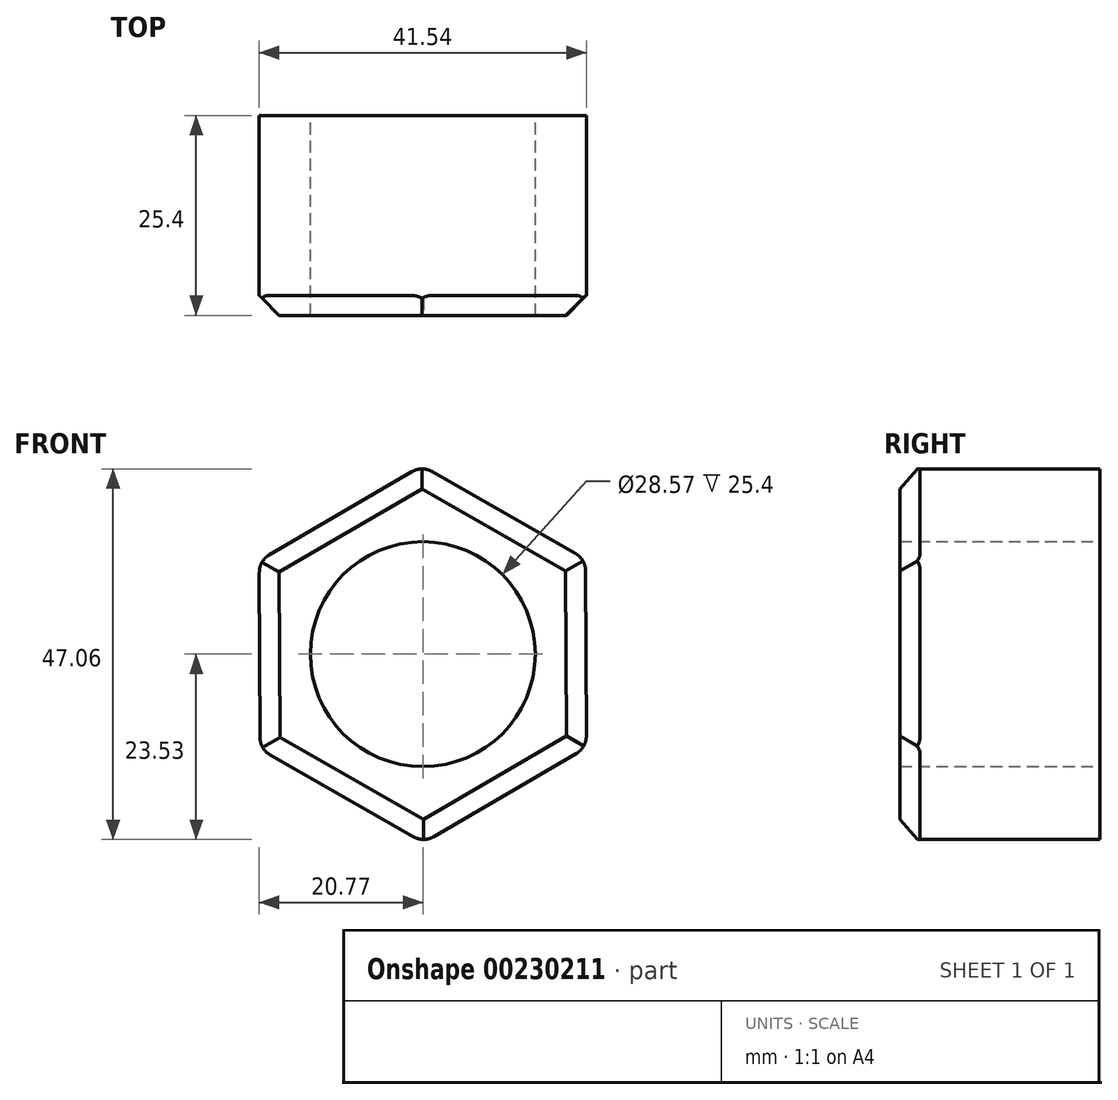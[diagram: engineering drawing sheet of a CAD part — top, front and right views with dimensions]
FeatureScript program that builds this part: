
annotation { "Feature Type Name" : "Feature", "Feature Type Description" : "" }
export const myFeature = defineFeature(function(context is Context, id is Id, definition is map)
    precondition{}
    {
        {
            var Q0;
            Q0=qCreatedBy(makeId("Front.planeOp"),FACE);
            var sketch = newSketch(context, id + "F0", { "sketchPlane" : qUnion([Q0])});
            skCircle(sketch, "E0", {"center": v(0, 0) * mm, "radius": 14.29 * mm});
            skCircle(sketch, "E1.cCircle", {"center": v(0, 0) * mm, "radius": 20.72 * mm, "construction": true});
            skLineSegment(sketch, "E1.0", {"start": v(-0.1, 23.93) * mm, "end": v(20.67, 12.06) * mm});
            skLineSegment(sketch, "E1.1", {"start": v(20.67, 12.06) * mm, "end": v(20.77, -11.87) * mm});
            skLineSegment(sketch, "E1.2", {"start": v(20.77, -11.87) * mm, "end": v(0.1, -23.93) * mm});
            skLineSegment(sketch, "E1.3", {"start": v(0.1, -23.93) * mm, "end": v(-20.67, -12.06) * mm});
            skLineSegment(sketch, "E1.4", {"start": v(-20.67, -12.06) * mm, "end": v(-20.77, 11.87) * mm});
            skLineSegment(sketch, "E1.5", {"start": v(-20.77, 11.87) * mm, "end": v(-0.1, 23.93) * mm});
            skPoint(sketch, "E1.0.midPoint", {"position": v(10.28, 18) * mm});
            skSolve(sketch);
        }
        {
            var Q0;
            Q0 = qSketchRegion(id + "F0", true);
            extrude(context, id + "F1", {"entities" : qUnion([Q0]), "depth" : 25.4 * mm});
        }
        {
            var Q0;
            Q0=makeQuery(id+"F1.opExtrude","CAP_EDGE",EDGE,{"disambiguationData":[OSD([sQuery(id+"F0.wireOp",EDGE,"E1.5")])],"isStart":false});
            var Q1;
            Q1=makeQuery(id+"F1.opExtrude","CAP_EDGE",EDGE,{"disambiguationData":[OSD([sQuery(id+"F0.wireOp",EDGE,"E1.4")])],"isStart":false});
            var Q2;
            Q2=makeQuery(id+"F1.opExtrude","CAP_EDGE",EDGE,{"disambiguationData":[OSD([sQuery(id+"F0.wireOp",EDGE,"E1.3")])],"isStart":false});
            var Q3;
            Q3=makeQuery(id+"F1.opExtrude","CAP_EDGE",EDGE,{"disambiguationData":[OSD([sQuery(id+"F0.wireOp",EDGE,"E1.2")])],"isStart":false});
            var Q4;
            Q4=makeQuery(id+"F1.opExtrude","CAP_EDGE",EDGE,{"disambiguationData":[OSD([sQuery(id+"F0.wireOp",EDGE,"E1.1")])],"isStart":false});
            var Q5;
            Q5=makeQuery(id+"F1.opExtrude","CAP_EDGE",EDGE,{"disambiguationData":[OSD([sQuery(id+"F0.wireOp",EDGE,"E1.0")])],"isStart":false});
            chamfer(context, id + "F2", {"entities" : qUnion([Q0, Q1, Q2, Q3, Q4, Q5]), "width" : 2.54 * mm, "tangentPropagation" : true});
        }
        {
            var Q0;
            Q0=makeQuery(id+"F1.opExtrude","SWEPT_EDGE",EDGE,{"disambiguationData":[OSD([sQuery(id+"F0.wireOp",EDGE,"E1.4"),sQuery(id+"F0.wireOp",EDGE,"E1.5")])]});
            var Q1;
            Q1=makeQuery(id+"F1.opExtrude","SWEPT_EDGE",EDGE,{"disambiguationData":[OSD([sQuery(id+"F0.wireOp",EDGE,"E1.0"),sQuery(id+"F0.wireOp",EDGE,"E1.5")])]});
            var Q2;
            Q2=makeQuery(id+"F1.opExtrude","SWEPT_EDGE",EDGE,{"disambiguationData":[OSD([sQuery(id+"F0.wireOp",EDGE,"E1.3"),sQuery(id+"F0.wireOp",EDGE,"E1.4")])]});
            var Q3;
            Q3=makeQuery(id+"F1.opExtrude","SWEPT_EDGE",EDGE,{"disambiguationData":[OSD([sQuery(id+"F0.wireOp",EDGE,"E1.2"),sQuery(id+"F0.wireOp",EDGE,"E1.3")])]});
            var Q4;
            Q4=makeQuery(id+"F1.opExtrude","SWEPT_EDGE",EDGE,{"disambiguationData":[OSD([sQuery(id+"F0.wireOp",EDGE,"E1.1"),sQuery(id+"F0.wireOp",EDGE,"E1.2")])]});
            var Q5;
            Q5=makeQuery(id+"F1.opExtrude","SWEPT_EDGE",EDGE,{"disambiguationData":[OSD([sQuery(id+"F0.wireOp",EDGE,"E1.0"),sQuery(id+"F0.wireOp",EDGE,"E1.1")])]});
            fillet(context, id + "F3", {"entities" : qUnion([Q0, Q1, Q2, Q3, Q4, Q5]), "radius" : 2.54 * mm, "tangentPropagation" : true, "allowEdgeOverflow" : false});
        }
    });
